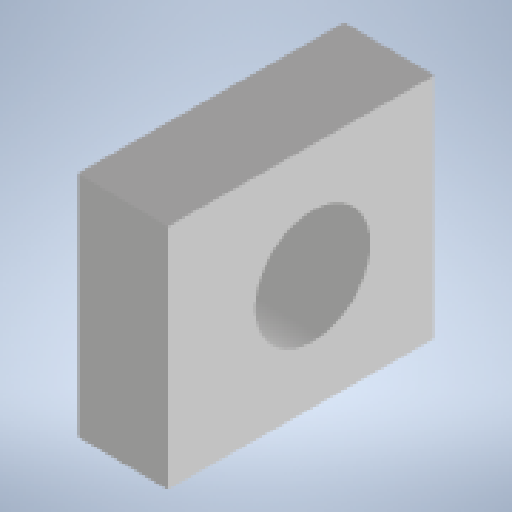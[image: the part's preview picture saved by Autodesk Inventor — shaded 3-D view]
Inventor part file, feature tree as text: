
AUTODESK INVENTOR PART (.ipt)
format: ipt  version: 2025 (Build 290162010, 162A)  size: 134,656 bytes
history: native  units: mm
features: other x4, sketch x3, extrude x2, hole x1, reference x1, projected_geometry x1
ambient origin geometry x8: Origin, YZ Plane, XZ Plane, XY Plane, X Axis, Y Axis, Z Axis, Center Point
bodies: Volumenkörper1 (feature_tree)
feature tree (12):
  extrude  "Extrusion1"  TaperAngle=0.0deg  [1 undecoded]
  extrude  "Extrusion2"  Depth=1.0mm
  hole  "Bohrung1"  [1 undecoded]
  sketch  "Skizze1"  dims[d0=10.0mm d1=0.0mm d2=0.0mm d3=0.0mm]
  reference  "Referenz2"
  sketch  "Skizze2"  dims[d4=5.0mm d5=6.0mm d6=5.0mm d7=2.0mm d8=90.0deg d9=8.0mm d10=20.594885mm d11=1.0mm]
  projected_geometry  "Projizierte Kontur1"
  sketch  "Skizze3"
  other  "<userpath>\GIT\HDVKBM\CAD\Krandemonstrator\Demonstrator.iam"
  other  "Demonstrator.iam"
  other  "UmlenkrolleHalterEinfachAngle:1"
  other  "HalterUmlenkrolleOVL:1"
note: 2 required parameter values undecoded (feature->parameter linkage not recoverable at this tier; creation-order binding heuristic only, values carry confidence <= 0.55)
